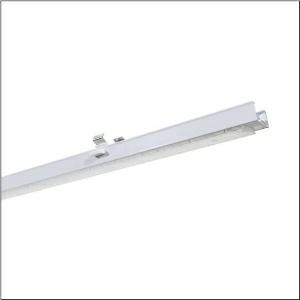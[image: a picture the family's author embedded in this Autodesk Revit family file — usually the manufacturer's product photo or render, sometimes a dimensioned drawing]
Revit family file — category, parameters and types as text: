
# Revit family: sanierungs-leuchteneinsatz_31_gen_2_51re12db49b_0821
name_source: partatom
category: Lighting Fixtures
units: mm (PartAtom-declared; Revit-internal decimal feet)

## family parameters
Cut with Voids When Loaded = No
Host = Face
Light Source = No
Part Type = Normal
Room Calculation Point = No
Round Connector Dimension = Use Diameter
Shared = No

## types (1)
- --- (1 x LED, 8900 lm, 56 W, 4000K)
    Apparent Load = 56 VA
    CIE Flux Codes = 65 91 98 99 100
    Color Rendering = 80
    Color Temperature = 4000K
    Default Elevation = 1800 mm
    Description = Refurbishment luminaire insert Gen.2, luminaire insert, of extruded aluminium section, coated, traffic white (RAL 9016), length: 1.472mm, width: 91mm, height: 53mm, LED rated luminous flux: 8.900lm, light colour: 840, control gear: DALI 2, with system connector: socket, mains connection: 220..240V, AC, 50/60Hz, primary light control with lens, of plastic, primary optical cover: cover, of PMMA, light emission: direct distribution, protection rating (complete): IP20, insulation class (complete): insulation class I (protective earthing), certification: CE, UKCA, impact resistance: IK02, permissible ambient temperature for indoor applications: -20..+40°C, packaging unit: 1 piece
    Height = 58 mm
    Lamp = 1 x LED
    Lamp Light Flux = 8900 lm
    Lamp Power = 56 W
    Lamp count = 1
    Length = 1472 mm
    Luminous efficacy = 159 lm/W
    Manufacturer = Siteco
    ModVariant = No
    Model = 51RE12DB49B
    Mounting Place = Ceiling
    Mounting Type = Pendant
    Number of Poles = 1
    OnlyDefault = Yes
    Power Factor = 1
    Product Name = Sanierungs-Leuchteneinsatz 31 Gen.2
    Product group = luminaire insert
    ProductGroupID = 902
    Protection Class = Protection class I
    Protection Degree = IP 20
    RLX_Detail_Level = 1
    RlxData = <blob elided: 21781 chars, md5=22f75a7d>
    Socket = socket
    Standby Power = 0 W
    System Light Flux = 8900 lm
    System Power = 56 W
    Type Comments = individual setting: luminous flux: 100 % | (OFF | ON | OFF | OFF) | 1200 mA
    Type Image = l_1266702.jpg
    URL = http://relux.com
    VarID = @adj_049483
    Voltage = 0 V
    Weight = 0.00 kg
    Width = 65 mm

## geometry (parser evidence)
native form markers: Blend x4, Sweep x11
no freeform markers — native parametric forms only
